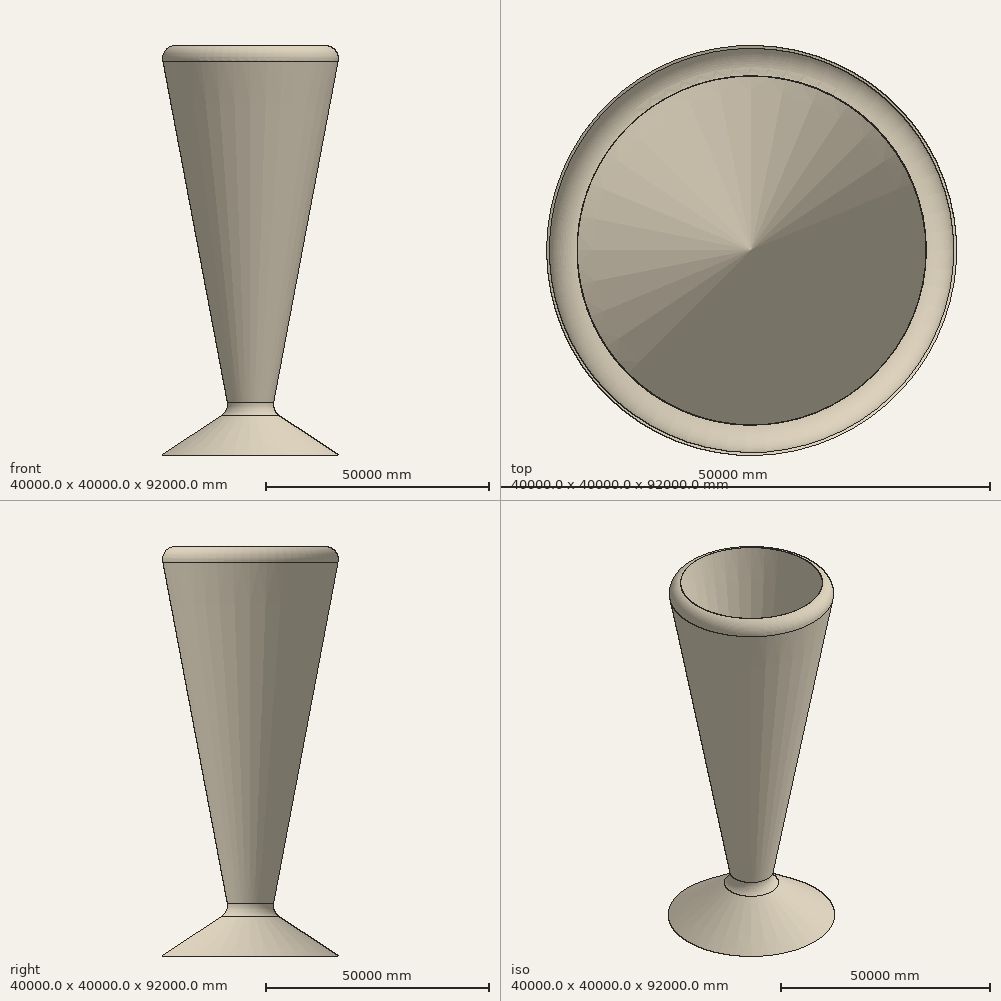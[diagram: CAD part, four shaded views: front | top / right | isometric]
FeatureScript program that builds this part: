
annotation { "Feature Type Name" : "Feature", "Feature Type Description" : "" }
export const myFeature = defineFeature(function(context is Context, id is Id, definition is map)
    precondition{}
    {
        {
            var Q0;
            Q0=qCreatedBy(makeId("Front.planeOp"),FACE);
            var sketch = newSketch(context, id + "F0", { "sketchPlane" : qUnion([Q0])});
            skLineSegment(sketch, "E0", {"start": v(-17000, 60000) * mm, "end": v(0, -30000) * mm});
            skLineSegment(sketch, "E1", {"start": v(0, -30000) * mm, "end": v(0, 60000) * mm});
            skLineSegment(sketch, "E2", {"start": v(-4844.44, -22000) * mm, "end": v(-20264.22, 59634.1) * mm});
            skLineSegment(sketch, "E3", {"start": v(-20264.22, 59634.1) * mm, "end": v(-17000, 60000) * mm});
            skPoint(sketch, "E4.orphan", {"position": v(-5666.67, 0) * mm});
            skLineSegment(sketch, "E5", {"start": v(-20000, -32000) * mm, "end": v(-4844.44, -22000) * mm});
            skLineSegment(sketch, "E6", {"start": v(-20000, -32000) * mm, "end": v(0, -32000) * mm});
            skLineSegment(sketch, "E7", {"start": v(0, -32000) * mm, "end": v(0, -30000) * mm});
            skSolve(sketch);
        }
        {
            var Q0;
            Q0 = qSketchRegion(id + "F0", true);
            var Q1;
            Q1=sQuery(id+"F0.wireOp",EDGE,"E1");
            revolve(context, id + "F1", {"surfaceOperationType" : NewSurfaceOperationType.NEW, "entities" : qUnion([Q0]), "axis" : qUnion([Q1]), "revolveType" : RevolveType.FULL});
        }
        {
            var Q0;
            Q0=makeQuery(id+"F1.opRevolve","SWEPT_EDGE",EDGE,{"disambiguationData":[OSD([sQuery(id+"F0.wireOp",EDGE,"E2"),sQuery(id+"F0.wireOp",EDGE,"E3")])]});
            fillet(context, id + "F2", {"entities" : qUnion([Q0]), "radius" : 3000 * mm, "tangentPropagation" : true, "allowEdgeOverflow" : false});
        }
        {
            var Q0;
            Q0=makeQuery(id+"F1.opRevolve","SWEPT_EDGE",EDGE,{"disambiguationData":[OSD([sQuery(id+"F0.wireOp",EDGE,"E2"),sQuery(id+"F0.wireOp",EDGE,"E5")])]});
            fillet(context, id + "F3", {"entities" : qUnion([Q0]), "radius" : 3000 * mm, "tangentPropagation" : true, "allowEdgeOverflow" : false});
        }
    });
